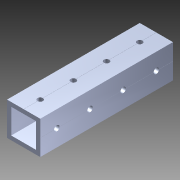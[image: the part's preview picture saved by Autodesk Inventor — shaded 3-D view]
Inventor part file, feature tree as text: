
AUTODESK INVENTOR PART (.ipt)
format: ipt  version: 2014 (Build 180170000, 170)  size: 1,117,184 bytes
history: native  units: in
note: dims shown in document units (in); Inventor stores cm internally (conversion verified against a paired STEP export)
features: pattern_circular x1, other x1, plane x1, extrude x1, imported_body x1, sketch x1
ambient origin geometry x8: Origin, YZ Plane, XZ Plane, XY Plane, X Axis, Y Axis, Z Axis, Center Point
bodies: Body1 (feature_tree)
feature tree (6):
  pattern_circular  "CirPattern2"
  other  "217-3426-STEP1"
  plane  "Work Plane1"
  extrude  "Extrusion1"  Depth=3937.0079in TaperAngle=0.0deg
  imported_body  "Base1"
  sketch  "Sketch1"  dims[d0=-4.0in d1=3937.0079in d2=0.0in]
